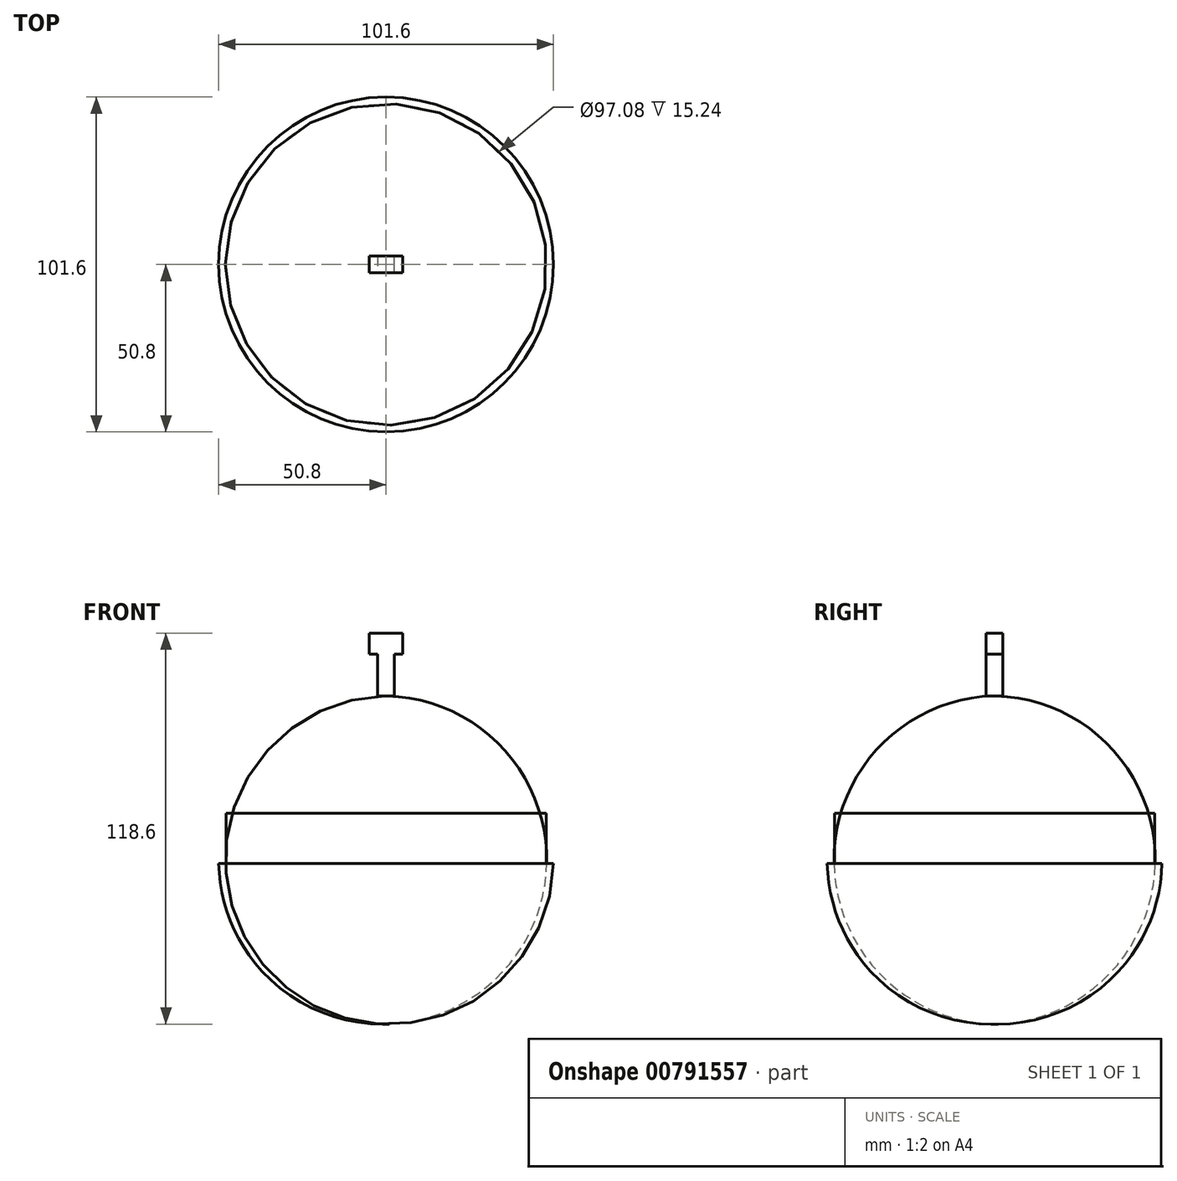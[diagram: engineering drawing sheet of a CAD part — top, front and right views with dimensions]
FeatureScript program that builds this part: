
annotation { "Feature Type Name" : "Feature", "Feature Type Description" : "" }
export const myFeature = defineFeature(function(context is Context, id is Id, definition is map)
    precondition{}
    {
        {
            var Q0;
            Q0=qCreatedBy(makeId("Front.planeOp"),FACE);
            var sketch = newSketch(context, id + "F0", { "sketchPlane" : qUnion([Q0])});
            skLineSegment(sketch, "E0", {"start": v(0, 0) * mm, "end": v(0, 50.8) * mm});
            skLineSegment(sketch, "E1", {"start": v(0, 50.8) * mm, "end": v(0, 0) * mm});
            skLineSegment(sketch, "E2", {"start": v(0, 0) * mm, "end": v(50.8, 0) * mm});
            skArc(sketch, "E3", {"start": v(50.8, 0) * mm, "mid": v(36.23, 36.23) * mm, "end": v(0, 50.8) * mm});
            skSolve(sketch);
        }
        {
            var Q0;
            Q0 = qSketchRegion(id + "F0", true);
            var Q1;
            Q1=sQuery(id+"F0.wireOp",EDGE,"E1");
            revolve(context, id + "F1", {"surfaceOperationType" : NewSurfaceOperationType.NEW, "entities" : qUnion([Q0]), "axis" : qUnion([Q1]), "revolveType" : RevolveType.FULL});
        }
        {
            var Q0;
            Q0=qCreatedBy(makeId("Top.planeOp"),FACE);
            var sketch = newSketch(context, id + "F2", { "sketchPlane" : qUnion([Q0])});
            skLineSegment(sketch, "E4", {"start": v(-51.08, 0) * mm, "end": v(-48.54, 0) * mm});
            skCircle(sketch, "E5", {"center": v(0, 0) * mm, "radius": 48.54 * mm});
            skSolve(sketch);
        }
        {
            var Q0;
            Q0 = qSketchRegion(id + "F2", true);
            extrude(context, id + "F3", {"entities" : qUnion([Q0]), "operationType" : NewBodyOperationType.REMOVE, "depth" : 15.24 * mm, "offsetDistance" : 25.4 * mm});
        }
        {
            var Q0;
            Q0=qCreatedBy(makeId("Top.planeOp"),FACE);
            var sketch = newSketch(context, id + "F4", { "sketchPlane" : qUnion([Q0])});
            skLineSegment(sketch, "E6", {"start": v(2.54, 0) * mm, "end": v(2.54, 2.54) * mm});
            skLineSegment(sketch, "E7", {"start": v(2.54, 2.54) * mm, "end": v(-2.54, 2.54) * mm});
            skLineSegment(sketch, "E8", {"start": v(-2.54, 2.54) * mm, "end": v(-2.54, -2.54) * mm});
            skLineSegment(sketch, "E9", {"start": v(-2.54, -2.54) * mm, "end": v(2.54, -2.54) * mm});
            skLineSegment(sketch, "E10", {"start": v(2.54, -2.54) * mm, "end": v(2.54, 0) * mm});
            skSolve(sketch);
        }
        {
            var Q0;
            Q0 = qSketchRegion(id + "F4", true);
            extrude(context, id + "F5", {"entities" : qUnion([Q0]), "operationType" : NewBodyOperationType.ADD, "depth" : 63.5 * mm, "offsetDistance" : 25.4 * mm, "hasSecondDirection" : true, "secondDirectionOppositeDirection" : false, "secondDirectionDepth" : 44.7 * mm});
        }
        {
            var Q0;
            Q0=makeQuery(id+"F5.opExtrude","CAP_FACE",FACE,{"disambiguationData":[OSD([sQuery(id+"F4.wireOp",EDGE,"E6"),sQuery(id+"F4.wireOp",EDGE,"E7"),sQuery(id+"F4.wireOp",EDGE,"E8"),sQuery(id+"F4.wireOp",EDGE,"E9"),sQuery(id+"F4.wireOp",EDGE,"E10")])],"isStart":false});
            var sketch = newSketch(context, id + "F6", { "sketchPlane" : qUnion([Q0])});
            skLineSegment(sketch, "E11", {"start": v(2.54, 2.54) * mm, "end": v(5.08, 2.54) * mm});
            skLineSegment(sketch, "E12", {"start": v(5.08, 2.54) * mm, "end": v(5.08, -2.54) * mm});
            skLineSegment(sketch, "E13", {"start": v(5.08, -2.54) * mm, "end": v(-2.54, -2.54) * mm});
            skLineSegment(sketch, "E14", {"start": v(-2.54, -2.54) * mm, "end": v(-5.08, -2.54) * mm});
            skLineSegment(sketch, "E15", {"start": v(-5.08, -2.54) * mm, "end": v(-5.08, 2.54) * mm});
            skLineSegment(sketch, "E16", {"start": v(-5.08, 2.54) * mm, "end": v(-2.54, 2.54) * mm});
            skSolve(sketch);
        }
        {
            var Q0;
            Q0 = qSketchRegion(id + "F6", true);
            var Q1;
            Q1=makeQuery(id+"F6.imprint","IMPRINT",FACE,{"disambiguationData":[TD([[makeQuery(id+"F6.imprint","IMPRINT",EDGE,{"derivedFrom":sQuery(id+"F6.wireOp",EDGE,"E14")}),-1.0]])]});
            var Q2;
            Q2=makeQuery(id+"F6.imprint","IMPRINT",FACE,{"disambiguationData":[TD([[makeQuery(id+"F6.imprint","IMPRINT",EDGE,{"derivedFrom":sQuery(id+"F6.wireOp",EDGE,"E11")}),-1.0]])]});
            var Q3;
            Q3=makeQuery(id+"F6.imprint","IMPRINT",FACE,{"disambiguationData":[TD([[makeQuery(id+"F6.imprint","IMPRINT",EDGE,{"derivedFrom":makeQuery(id+"F5.opExtrude","CAP_EDGE",EDGE,{"disambiguationData":[OSD([sQuery(id+"F4.wireOp",EDGE,"E7")])],"isStart":false})}),1.0]])]});
            extrude(context, id + "F7", {"entities" : qUnion([Q0, Q1, Q2, Q3]), "operationType" : NewBodyOperationType.ADD, "depth" : 6.35 * mm, "offsetDistance" : 25.4 * mm});
        }
        {
            var Q0;
            Q0 = qSketchRegion(id + "F4", true);
            extrude(context, id + "F8", {"entities" : qUnion([Q0]), "operationType" : NewBodyOperationType.REMOVE, "oppositeDirection" : true, "depth" : 50.8 * mm, "offsetDistance" : 25.4 * mm});
        }
    });
